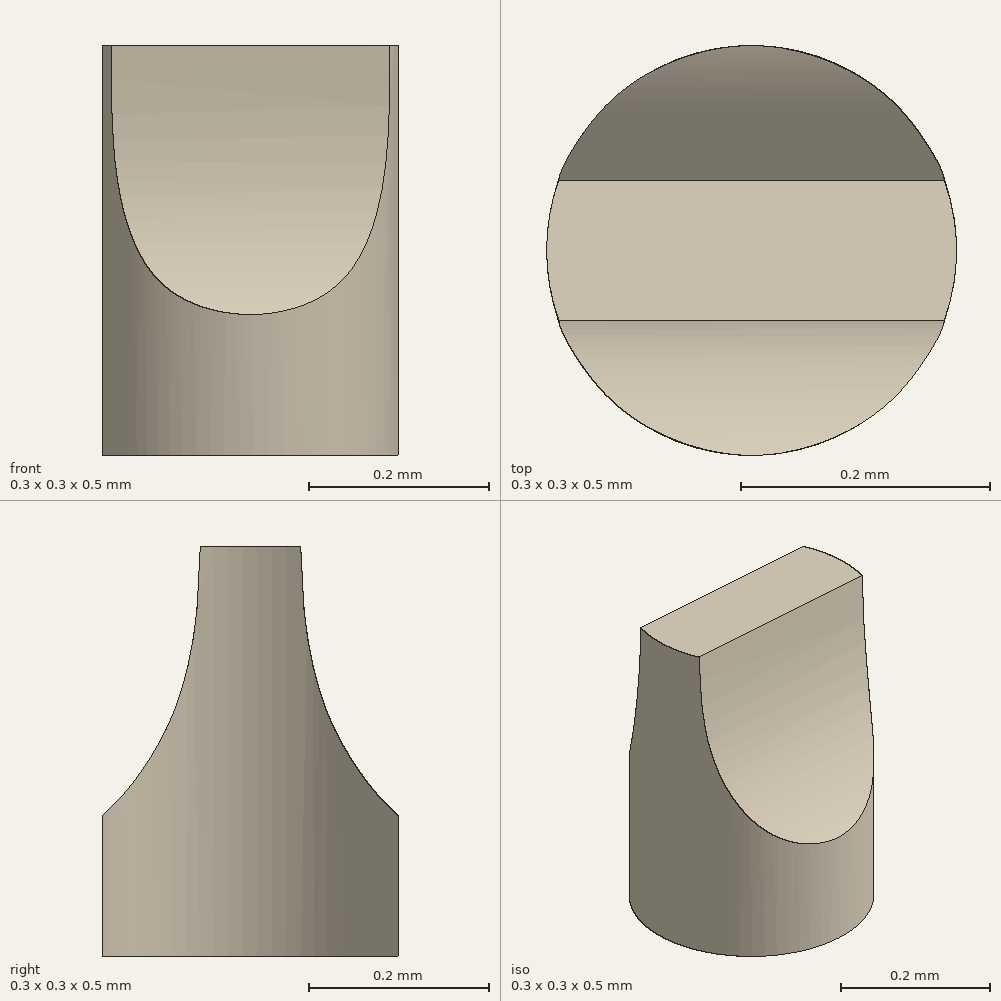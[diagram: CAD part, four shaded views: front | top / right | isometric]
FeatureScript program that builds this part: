
annotation { "Feature Type Name" : "Feature", "Feature Type Description" : "" }
export const myFeature = defineFeature(function(context is Context, id is Id, definition is map)
    precondition{}
    {
        {
            var Q0;
            Q0=qCreatedBy(makeId("Right.planeOp"),FACE);
            var sketch = newSketch(context, id + "F0", { "sketchPlane" : qUnion([Q0])});
            skLineSegment(sketch, "E0.bottom", {"start": v(0, 0) * mm, "end": v(0.17, 0) * mm});
            skLineSegment(sketch, "E0.top", {"start": v(0, 0.46) * mm, "end": v(0.17, 0.46) * mm});
            skLineSegment(sketch, "E0.left", {"start": v(0, 0) * mm, "end": v(0, 0.46) * mm});
            skLineSegment(sketch, "E0.right", {"start": v(0.17, 0) * mm, "end": v(0.17, 0.46) * mm});
            skSolve(sketch);
        }
        {
            var Q0;
            Q0=makeQuery(id+"F0.imprint","IMPRINT",FACE,{"disambiguationData":[TD([[makeQuery(id+"F0.imprint","IMPRINT",EDGE,{"derivedFrom":sQuery(id+"F0.wireOp",EDGE,"E0.bottom")}),1.0]])]});
            var Q1;
            Q1=sQuery(id+"F0.wireOp",EDGE,"E0.left");
            revolve(context, id + "F1", {"entities" : qUnion([Q0]), "axis" : qUnion([Q1]), "revolveType" : RevolveType.FULL});
        }
        {
            var Q0;
            Q0=qCreatedBy(makeId("Right.planeOp"),FACE);
            var sketch = newSketch(context, id + "F2", { "sketchPlane" : qUnion([Q0])});
            skFitSpline(sketch, "E1", {"points": [v(0.06, 0.47) * mm, v(0.2, 0.13) * mm], "startDerivative": vector(0, -0.53) * mm, "endDerivative": vector(0.31, -0.22) * mm});
            skLineSegment(sketch, "E2", {"start": v(0.2, 0.13) * mm, "end": v(0.38, 0) * mm, "construction": true});
            skLineSegment(sketch, "E3", {"start": v(0.2, 0.13) * mm, "end": v(0.2, 0.47) * mm});
            skLineSegment(sketch, "E4", {"start": v(0.2, 0.47) * mm, "end": v(0.06, 0.47) * mm});
            skFitSpline(sketch, "E5.MirrorCS", {"points": [v(-0.06, 0.47) * mm, v(-0.2, 0.13) * mm], "startDerivative": vector(0, -0.53) * mm, "endDerivative": vector(-0.31, -0.22) * mm});
            skLineSegment(sketch, "E6.MirrorCS", {"start": v(-0.2, 0.13) * mm, "end": v(-0.2, 0.47) * mm});
            skLineSegment(sketch, "E7.MirrorCS", {"start": v(-0.2, 0.47) * mm, "end": v(-0.06, 0.47) * mm});
            skSolve(sketch);
        }
        {
            var Q0;
            Q0=makeQuery(id+"F2.imprint","IMPRINT",FACE,{"disambiguationData":[TD([[makeQuery(id+"F2.imprint","IMPRINT",EDGE,{"derivedFrom":sQuery(id+"F2.wireOp",EDGE,"E5.MirrorCS")}),-1.0]])]});
            var Q1;
            Q1=makeQuery(id+"F2.imprint","IMPRINT",FACE,{"disambiguationData":[TD([[makeQuery(id+"F2.imprint","IMPRINT",EDGE,{"derivedFrom":sQuery(id+"F2.wireOp",EDGE,"E1")}),1.0]])]});
            extrude(context, id + "F3", {"entities" : qUnion([Q0, Q1]), "operationType" : NewBodyOperationType.REMOVE, "oppositeDirection" : true, "depth" : 0.5 * mm, "symmetric" : true});
        }
    });
